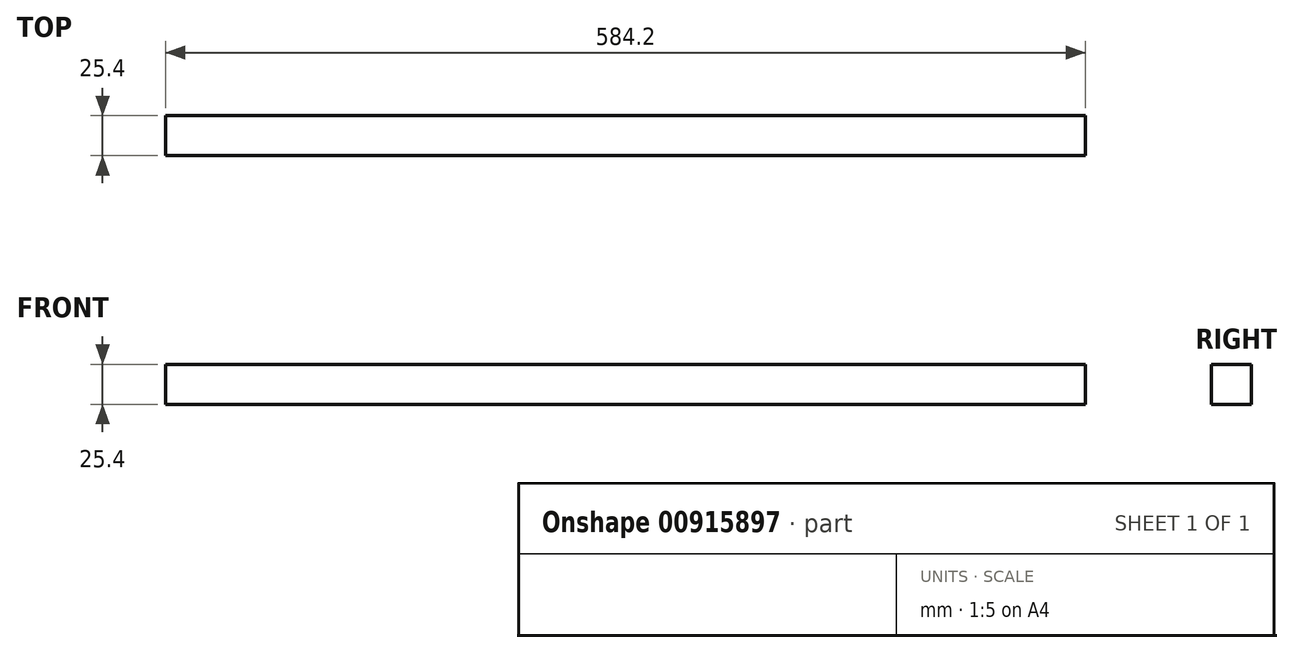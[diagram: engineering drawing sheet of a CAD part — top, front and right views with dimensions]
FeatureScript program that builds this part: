
annotation { "Feature Type Name" : "Feature", "Feature Type Description" : "" }
export const myFeature = defineFeature(function(context is Context, id is Id, definition is map)
    precondition{}
    {
        {
            var Q0;
            Q0=qCreatedBy(makeId("Front.planeOp"),FACE);
            var sketch = newSketch(context, id + "F0", { "sketchPlane" : qUnion([Q0])});
            skLineSegment(sketch, "E0.bottom", {"start": v(226.13, -32.4) * mm, "end": v(-358.07, -32.4) * mm});
            skLineSegment(sketch, "E0.top", {"start": v(226.13, -7) * mm, "end": v(-358.07, -7) * mm});
            skLineSegment(sketch, "E0.left", {"start": v(226.13, -32.4) * mm, "end": v(226.13, -7) * mm});
            skLineSegment(sketch, "E0.right", {"start": v(-358.07, -32.4) * mm, "end": v(-358.07, -7) * mm});
            skPoint(sketch, "E0.middle", {"position": v(-65.97, -19.7) * mm});
            skSolve(sketch);
        }
        {
            var Q0;
            Q0 = qSketchRegion(id + "F0", true);
            extrude(context, id + "F1", {"entities" : qUnion([Q0]), "endBound" : BoundingType.SYMMETRIC, "depth" : 25.4 * mm, "offsetDistance" : 25.4 * mm});
        }
    });
